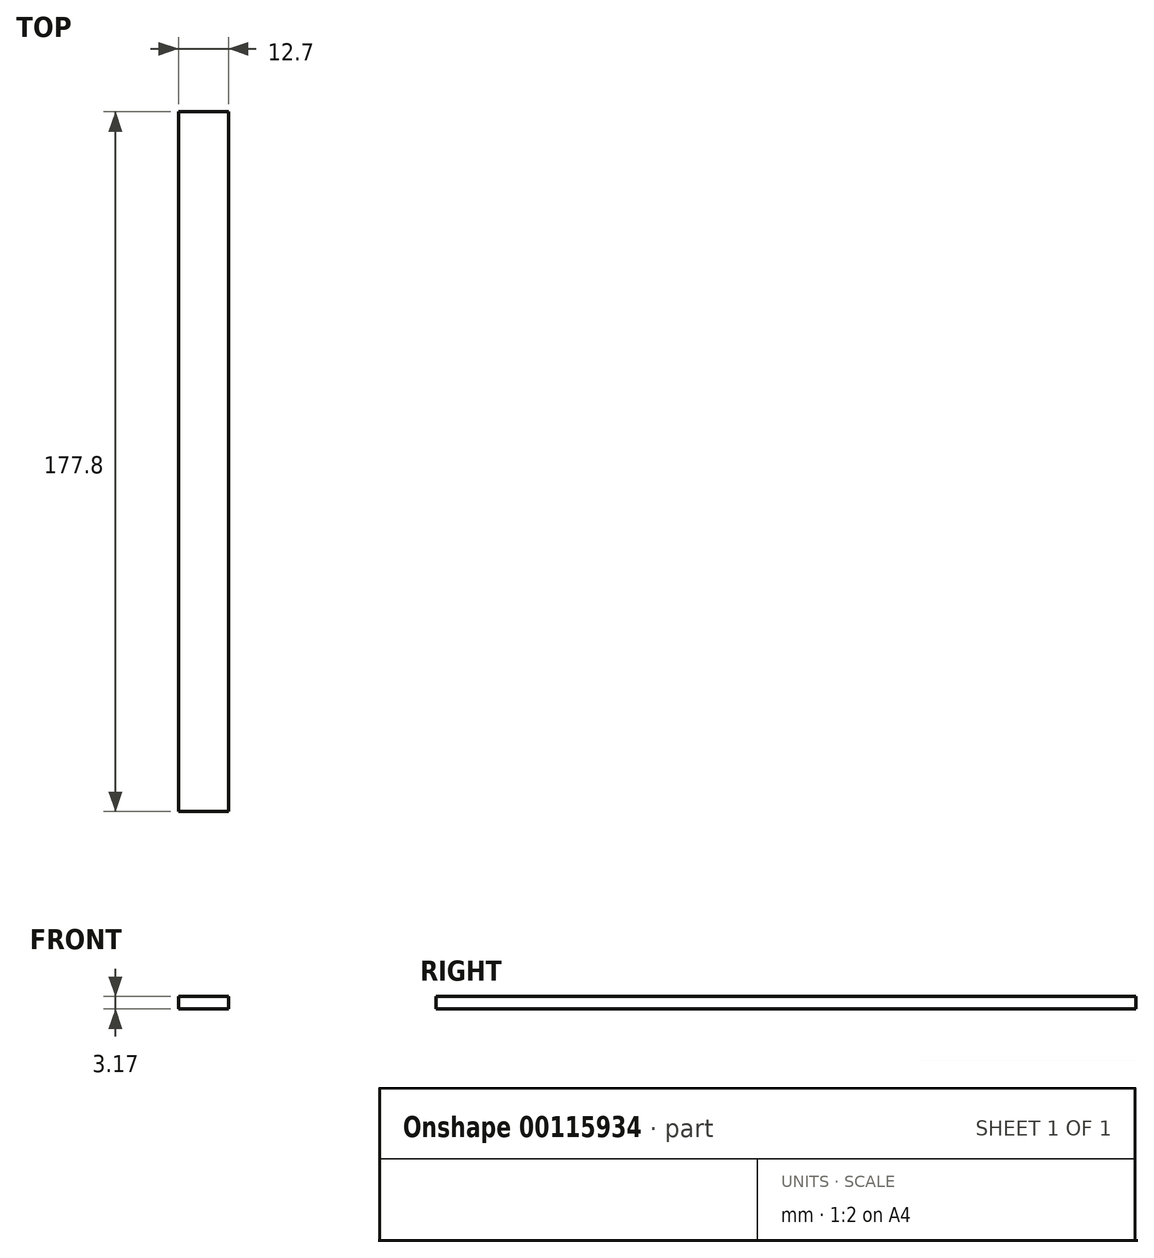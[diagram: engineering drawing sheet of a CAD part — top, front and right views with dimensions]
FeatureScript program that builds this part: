
annotation { "Feature Type Name" : "Feature", "Feature Type Description" : "" }
export const myFeature = defineFeature(function(context is Context, id is Id, definition is map)
    precondition{}
    {
        {
            var Q0;
            Q0=qCreatedBy(makeId("Top.planeOp"),FACE);
            var sketch = newSketch(context, id + "F0", { "sketchPlane" : qUnion([Q0])});
            skLineSegment(sketch, "E0.bottom", {"start": v(-16.97, 169.73) * mm, "end": v(-4.27, 169.73) * mm});
            skLineSegment(sketch, "E0.top", {"start": v(-16.97, -8.07) * mm, "end": v(-4.27, -8.07) * mm});
            skLineSegment(sketch, "E0.left", {"start": v(-16.97, 169.73) * mm, "end": v(-16.97, -8.07) * mm});
            skLineSegment(sketch, "E0.right", {"start": v(-4.27, 169.73) * mm, "end": v(-4.27, -8.07) * mm});
            skSolve(sketch);
        }
        {
            var Q0;
            Q0=makeQuery(id+"F0.imprint","IMPRINT",FACE,{"disambiguationData":[TD([[makeQuery(id+"F0.imprint","IMPRINT",EDGE,{"derivedFrom":sQuery(id+"F0.wireOp",EDGE,"E0.bottom")}),-1.0]])]});
            extrude(context, id + "F1", {"entities" : qUnion([Q0]), "depth" : 3.17 * mm});
        }
    });
